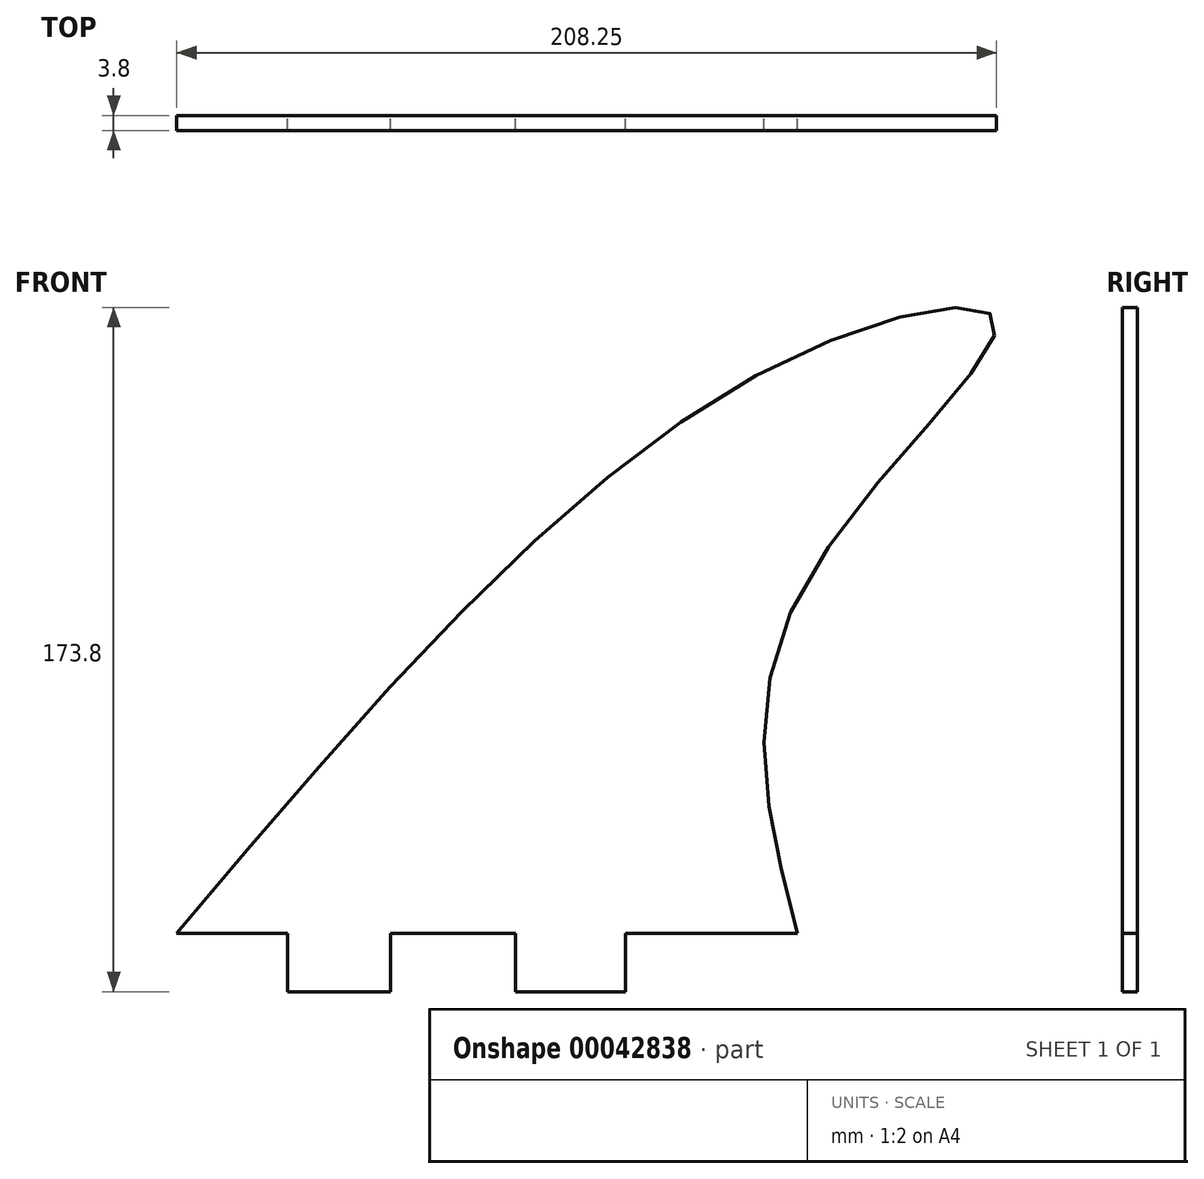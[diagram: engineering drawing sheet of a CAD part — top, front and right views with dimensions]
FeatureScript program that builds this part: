
annotation { "Feature Type Name" : "Feature", "Feature Type Description" : "" }
export const myFeature = defineFeature(function(context is Context, id is Id, definition is map)
    precondition{}
    {
        {
            var Q0;
            Q0=qCreatedBy(makeId("Front.planeOp"),FACE);
            var sketch = newSketch(context, id + "F0", { "sketchPlane" : qUnion([Q0])});
            skLineSegment(sketch, "E0", {"start": v(-75.5, -37.44) * mm, "end": v(-47.41, -37.44) * mm});
            skLineSegment(sketch, "E1", {"start": v(-47.41, -37.44) * mm, "end": v(-47.41, -52.3) * mm});
            skLineSegment(sketch, "E2", {"start": v(-47.41, -52.3) * mm, "end": v(-21.16, -52.3) * mm});
            skLineSegment(sketch, "E3", {"start": v(-21.16, -52.3) * mm, "end": v(-21.16, -37.44) * mm});
            skLineSegment(sketch, "E4", {"start": v(-21.16, -37.44) * mm, "end": v(10.58, -37.44) * mm});
            skLineSegment(sketch, "E5", {"start": v(10.58, -37.44) * mm, "end": v(10.58, -52.3) * mm});
            skLineSegment(sketch, "E6", {"start": v(10.58, -52.3) * mm, "end": v(38.46, -52.3) * mm});
            skLineSegment(sketch, "E7", {"start": v(38.46, -52.3) * mm, "end": v(38.46, -37.44) * mm});
            skLineSegment(sketch, "E8", {"start": v(38.46, -37.44) * mm, "end": v(82.21, -37.44) * mm});
            skFitSpline(sketch, "E9", {"points": [v(82.21, -37.44) * mm, v(82.21, 47.82) * mm, v(132.68, 117.62) * mm, v(74.56, 105.78) * mm, v(-75.5, -37.44) * mm], "startDerivative": vector(-98.04, 370.2) * mm, "endDerivative": vector(-414.62, -491.1) * mm});
            skSolve(sketch);
        }
        {
            var Q0;
            Q0=makeQuery(id+"F0.imprint","IMPRINT",FACE,{"disambiguationData":[TD([[makeQuery(id+"F0.imprint","IMPRINT",EDGE,{"derivedFrom":sQuery(id+"F0.wireOp",EDGE,"E0")}),1.0]])]});
            extrude(context, id + "F1", {"entities" : qUnion([Q0]), "depth" : 3.8 * mm});
        }
    });
